# Revit family: Bath-Freestanding-KOHLER-Sunstruck-K-EX34378T-1
name_source: partatom
category: Plumbing Fixtures
units: mm (PartAtom-declared; Revit-internal decimal feet)

## family parameters
Cut with Voids When Loaded = No
Host = Face
OmniClass Number = 23.31.15.00
OmniClass Title = Bathtubs
Part Type = Normal
Room Calculation Point = No
Round Connector Dimension = Use Diameter
Shared = No

## types (2) — shared parameters
ADA Compliant = No
Assembly Code = D2010500
CW Connection = No
Cold Water Inlet = Cold Water Inlet
Date Modified = 10/12/2023
Default Elevation = 0"
Drain Included = Yes
Finish = Kohler-Lithocast-HW1-Honed_White
HW Connection = No
Height = 23 1/16"
Hot Water Inlet = Hot Water Inlet
Length = 66 15/16"
Manufacturer = Kohler Co.
Master Format 2014 = 22 41 19
Master Format 2014 Name = Residential Bathtubs
Material = Lithocast
Product Name = Sunstruck
URL = http://www.kohler.com.cn
Vent Connection = No
Waste Connection = Yes
Waste Water Outlet = Waste Water Outlet
WaterSense Certified = No
Width = 29 1/2"

## per-type parameters (varying)
| type | Description | Model | Type | with grab | without grab |
| With Grab Rail, HW1-Honed White | 1.7M  Gel Coat Lithocast Bath With Grab Rail Hole | K-EX34378T-GRHL-HW1 | 2 | Yes | No |
| Without Grab Rail , HW1-Honed White | 1.7M Gel Coat Lithocast Bath | K-EX34378T-HW1 | 1 | No | Yes |

## geometry (parser evidence)
native form markers: Sweep x6
no freeform markers — native parametric forms only
